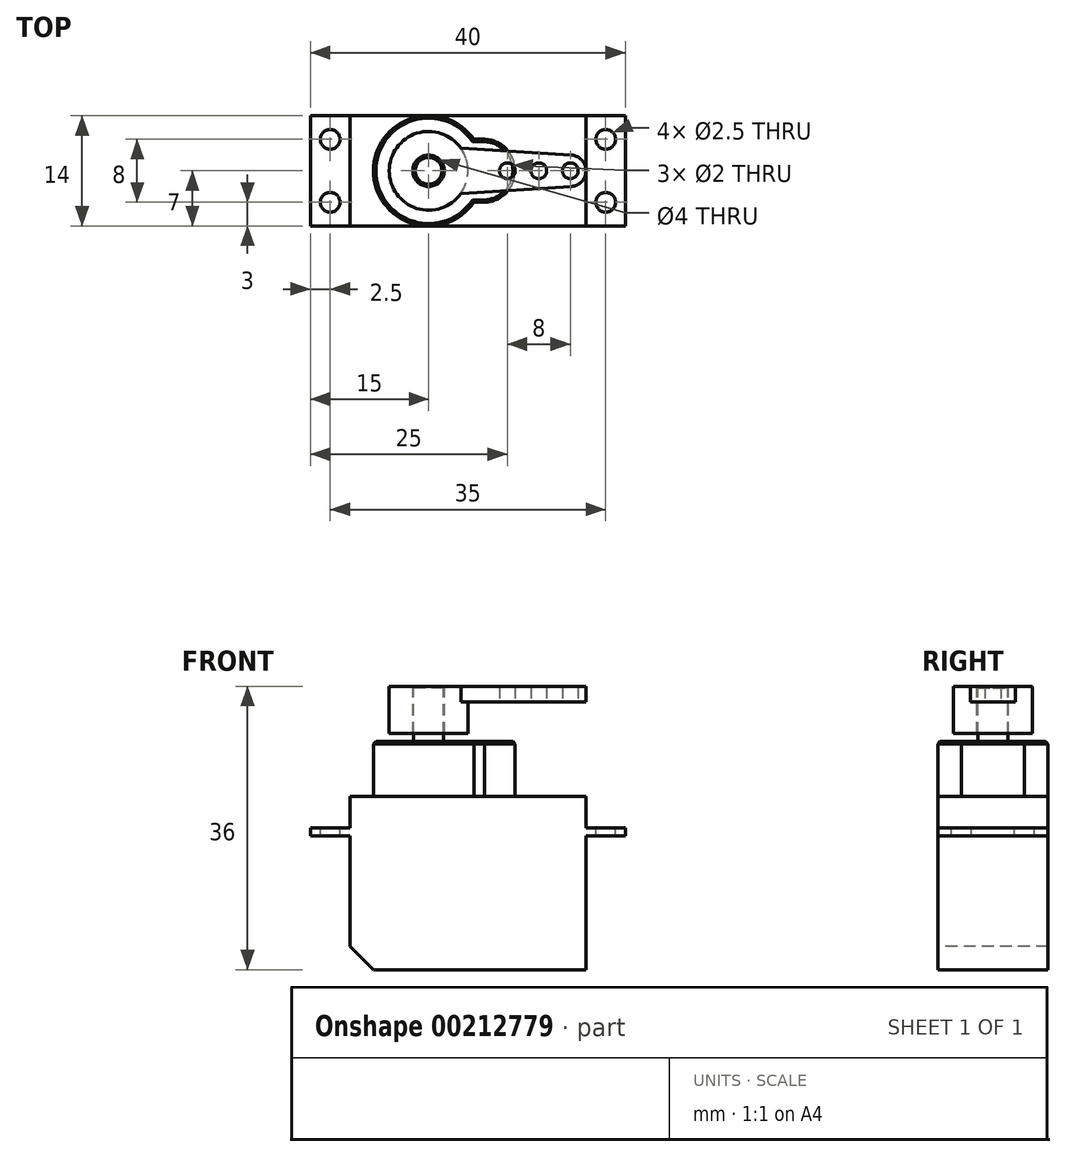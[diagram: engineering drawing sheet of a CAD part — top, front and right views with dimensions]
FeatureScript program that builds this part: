
annotation { "Feature Type Name" : "Feature", "Feature Type Description" : "" }
export const myFeature = defineFeature(function(context is Context, id is Id, definition is map)
    precondition{}
    {
        {
            var Q0;
            Q0=qCreatedBy(makeId("Top.planeOp"),FACE);
            var sketch = newSketch(context, id + "F0", { "sketchPlane" : qUnion([Q0])});
            skLineSegment(sketch, "E0", {"start": v(0, 0) * mm, "end": v(18, 0) * mm, "construction": true});
            skArc(sketch, "E1", {"start": v(4.1, 2.86) * mm, "mid": v(-5, 0) * mm, "end": v(4.1, -2.86) * mm});
            skCircle(sketch, "E2", {"center": v(18, 0) * mm, "radius": 1 * mm});
            skArc(sketch, "E3", {"start": v(18.12, -2) * mm, "mid": v(20, 0) * mm, "end": v(18.12, 2) * mm});
            skLineSegment(sketch, "E4", {"start": v(4.1, 2.86) * mm, "end": v(18.12, 2) * mm});
            skLineSegment(sketch, "E5.MirrorCS", {"start": v(4.1, -2.86) * mm, "end": v(18.12, -2) * mm});
            skCircle(sketch, "E6", {"center": v(14, 0) * mm, "radius": 1 * mm});
            skCircle(sketch, "E7", {"center": v(10, 0) * mm, "radius": 1 * mm});
            skSolve(sketch);
        }
        {
            var Q0;
            Q0 = qSketchRegion(id + "F0", true);
            extrude(context, id + "F1", {"entities" : qUnion([Q0]), "depth" : 2 * mm});
        }
        {
            var Q0;
            Q0=makeQuery(id+"F1.opExtrude","CAP_FACE",FACE,{"disambiguationData":[OSD([sQuery(id+"F0.wireOp",EDGE,"E1"),sQuery(id+"F0.wireOp",EDGE,"E2"),sQuery(id+"F0.wireOp",EDGE,"E3"),sQuery(id+"F0.wireOp",EDGE,"E4"),sQuery(id+"F0.wireOp",EDGE,"E5.MirrorCS"),sQuery(id+"F0.wireOp",EDGE,"E6"),sQuery(id+"F0.wireOp",EDGE,"E7")])],"isStart":true});
            var sketch = newSketch(context, id + "F2", { "sketchPlane" : qUnion([Q0])});
            skCircle(sketch, "E8", {"center": v(0, 0) * mm, "radius": 5 * mm});
            skSolve(sketch);
        }
        {
            var Q0;
            Q0 = qSketchRegion(id + "F2", true);
            extrude(context, id + "F3", {"entities" : qUnion([Q0]), "operationType" : NewBodyOperationType.ADD, "depth" : 4 * mm});
        }
        {
            var Q0;
            Q0=makeQuery(id+"F1.opExtrude","CAP_FACE",FACE,{"disambiguationData":[OSD([sQuery(id+"F0.wireOp",EDGE,"E1"),sQuery(id+"F0.wireOp",EDGE,"E2"),sQuery(id+"F0.wireOp",EDGE,"E3"),sQuery(id+"F0.wireOp",EDGE,"E4"),sQuery(id+"F0.wireOp",EDGE,"E5.MirrorCS"),sQuery(id+"F0.wireOp",EDGE,"E6"),sQuery(id+"F0.wireOp",EDGE,"E7")])],"isStart":false});
            var sketch = newSketch(context, id + "F4", { "sketchPlane" : qUnion([Q0])});
            skCircle(sketch, "E9", {"center": v(0, 0) * mm, "radius": 2 * mm});
            skSolve(sketch);
        }
        {
            var Q0;
            Q0=makeQuery(id+"F4.imprint","IMPRINT",FACE,{"disambiguationData":[TD([[makeQuery(id+"F4.imprint","IMPRINT",EDGE,{"derivedFrom":sQuery(id+"F4.wireOp",EDGE,"E9")}),1.0]])]});
            extrude(context, id + "F5", {"entities" : qUnion([Q0]), "operationType" : NewBodyOperationType.REMOVE, "oppositeDirection" : true, "depth" : 25 * mm});
        }
        {
            var Q0;
            Q0=makeQuery(id+"F1.opExtrude","CAP_FACE",FACE,{"disambiguationData":[OSD([sQuery(id+"F0.wireOp",EDGE,"E1"),sQuery(id+"F0.wireOp",EDGE,"E2"),sQuery(id+"F0.wireOp",EDGE,"E3"),sQuery(id+"F0.wireOp",EDGE,"E4"),sQuery(id+"F0.wireOp",EDGE,"E5.MirrorCS"),sQuery(id+"F0.wireOp",EDGE,"E6"),sQuery(id+"F0.wireOp",EDGE,"E7")])],"isStart":false});
            var sketch = newSketch(context, id + "F6", { "sketchPlane" : qUnion([Q0])});
            skCircle(sketch, "E10", {"center": v(0, 0) * mm, "radius": 1.9 * mm});
            skSolve(sketch);
        }
        {
            var Q0;
            Q0=makeQuery(id+"F6.imprint","IMPRINT",FACE,{"disambiguationData":[TD([[makeQuery(id+"F6.imprint","IMPRINT",EDGE,{"derivedFrom":sQuery(id+"F6.wireOp",EDGE,"E10")}),1.0]])]});
            extrude(context, id + "F7", {"entities" : qUnion([Q0]), "oppositeDirection" : true, "depth" : 10 * mm});
        }
        {
            var Q0;
            Q0=makeQuery(id+"F7.opExtrude","CAP_EDGE",EDGE,{"disambiguationData":[OSD([sQuery(id+"F6.wireOp",EDGE,"E10")])],"isStart":true});
            var Q1;
            Q1=makeQuery(id+"F5.boolean.opBoolean","COPY",EDGE,{"derivedFrom":makeQuery(id+"F5.opExtrude","CAP_EDGE",EDGE,{"disambiguationData":[OSD([sQuery(id+"F4.wireOp",EDGE,"E9")])],"isStart":true})});
            chamfer(context, id + "F8", {"entities" : qUnion([Q0, Q1]), "width" : 0.2 * mm, "tangentPropagation" : true});
        }
        {
            var Q0;
            Q0=qCreatedBy(makeId("Front.planeOp"),FACE);
            var sketch = newSketch(context, id + "F9", { "sketchPlane" : qUnion([Q0])});
            skLineSegment(sketch, "E11.bottom", {"start": v(20, -12) * mm, "end": v(-10, -12) * mm});
            skLineSegment(sketch, "E11.top", {"start": v(20, -34) * mm, "end": v(-10, -34) * mm});
            skLineSegment(sketch, "E11.left", {"start": v(20, -12) * mm, "end": v(20, -16) * mm});
            skLineSegment(sketch, "E11.right", {"start": v(-10, -12) * mm, "end": v(-10, -16) * mm});
            skPoint(sketch, "E11.middle", {"position": v(0, -24) * mm});
            skLineSegment(sketch, "E12.bottom", {"start": v(25, -17) * mm, "end": v(20, -17) * mm});
            skLineSegment(sketch, "E12.top", {"start": v(25, -16) * mm, "end": v(20, -16) * mm});
            skLineSegment(sketch, "E12.left", {"start": v(25, -17) * mm, "end": v(25, -16) * mm});
            skLineSegment(sketch, "E12.right", {"start": v(-15, -17) * mm, "end": v(-15, -16) * mm});
            skPoint(sketch, "E12.middle", {"position": v(0, -14.5) * mm});
            skLineSegment(sketch, "E13.trimOffspring", {"start": v(-10, -17) * mm, "end": v(-10, -34) * mm});
            skLineSegment(sketch, "E14.trimOffspring", {"start": v(20, -17) * mm, "end": v(20, -34) * mm});
            skLineSegment(sketch, "E15.trimOffspring", {"start": v(-10, -16) * mm, "end": v(-15, -16) * mm});
            skLineSegment(sketch, "E16.trimOffspring", {"start": v(-10, -17) * mm, "end": v(-15, -17) * mm});
            skSolve(sketch);
        }
        {
            var Q0;
            Q0 = qSketchRegion(id + "F9", true);
            extrude(context, id + "F10", {"entities" : qUnion([Q0]), "endBound" : BoundingType.SYMMETRIC, "depth" : 14 * mm});
        }
        {
            var Q0;
            Q0=makeQuery(id+"F10.opExtrude","SWEPT_FACE",FACE,{"disambiguationData":[OSD([sQuery(id+"F9.wireOp",EDGE,"E11.bottom")])]});
            var sketch = newSketch(context, id + "F11", { "sketchPlane" : qUnion([Q0])});
            skArc(sketch, "E17", {"start": v(5.75, 4) * mm, "mid": v(-7, 0) * mm, "end": v(5.75, -4) * mm});
            skArc(sketch, "E18", {"start": v(7.12, -4) * mm, "mid": v(11, 0) * mm, "end": v(7.12, 4) * mm});
            skLineSegment(sketch, "E19", {"start": v(7.12, 4) * mm, "end": v(5.75, 4) * mm});
            skLineSegment(sketch, "E20", {"start": v(7.12, -4) * mm, "end": v(5.75, -4) * mm});
            skSolve(sketch);
        }
        {
            var Q0;
            Q0 = qSketchRegion(id + "F11", true);
            extrude(context, id + "F12", {"entities" : qUnion([Q0]), "operationType" : NewBodyOperationType.ADD, "endBound" : BoundingType.SYMMETRIC, "depth" : 14 * mm});
        }
        {
            var Q0;
            Q0=makeQuery(id+"F12.opExtrude","CAP_EDGE",EDGE,{"disambiguationData":[OSD([sQuery(id+"F11.wireOp",EDGE,"E17")])],"isStart":false});
            var Q1;
            Q1=makeQuery(id+"F12.opExtrude","CAP_EDGE",EDGE,{"disambiguationData":[OSD([sQuery(id+"F11.wireOp",EDGE,"E20")])],"isStart":false});
            var Q2;
            Q2=makeQuery(id+"F12.opExtrude","CAP_EDGE",EDGE,{"disambiguationData":[OSD([sQuery(id+"F11.wireOp",EDGE,"E18")])],"isStart":false});
            var Q3;
            Q3=makeQuery(id+"F12.opExtrude","CAP_EDGE",EDGE,{"disambiguationData":[OSD([sQuery(id+"F11.wireOp",EDGE,"E19")])],"isStart":false});
            chamfer(context, id + "F13", {"entities" : qUnion([Q0, Q1, Q2, Q3]), "width" : .3 * mm, "tangentPropagation" : true});
        }
        {
            var Q0;
            Q0=makeQuery(id+"F10.opExtrude","SWEPT_FACE",FACE,{"disambiguationData":[OSD([sQuery(id+"F9.wireOp",EDGE,"E12.top")])]});
            var sketch = newSketch(context, id + "F14", { "sketchPlane" : qUnion([Q0])});
            skCircle(sketch, "E21", {"center": v(22.5, 4) * mm, "radius": 1.25 * mm});
            skLineSegment(sketch, "E22", {"start": v(0, 0) * mm, "end": v(31.48, 0) * mm, "construction": true});
            skPoint(sketch, "E22.endSnap0", {"position": v(20, 0) * mm});
            skCircle(sketch, "E23", {"center": v(-12.5, 4) * mm, "radius": 1.25 * mm});
            skCircle(sketch, "E24.MirrorC", {"center": v(22.5, -4) * mm, "radius": 1.25 * mm});
            skCircle(sketch, "E25.MirrorC", {"center": v(-12.5, -4) * mm, "radius": 1.25 * mm});
            skSolve(sketch);
        }
        {
            var Q0;
            Q0 = qSketchRegion(id + "F14", true);
            extrude(context, id + "F15", {"entities" : qUnion([Q0]), "operationType" : NewBodyOperationType.REMOVE, "endBound" : BoundingType.UP_TO_NEXT, "oppositeDirection" : true, "depth" : 25 * mm});
        }
        {
            var Q0;
            Q0=makeQuery(id+"F10.opExtrude","SWEPT_EDGE",EDGE,{"disambiguationData":[OSD([sQuery(id+"F9.wireOp",EDGE,"E11.top"),sQuery(id+"F9.wireOp",EDGE,"E13.trimOffspring")])]});
            chamfer(context, id + "F16", {"entities" : qUnion([Q0]), "width" : 3 * mm, "tangentPropagation" : true});
        }
    });
